# Revit family: Ytong stropní a střešní nosník
name_source: partatom
category: Konstrukční rámová konstrukce
units: mm (PartAtom-declared; Revit-internal decimal feet)

## family parameters
Materiál pro modelové chování = Jiné
Ořezat dutým tvarem při načtení = Ne
Sdílené = Ne
Tvar řezu = Není definováno
Vždy exportovat jako geometrii = Ne
Vždy vertikální = Ano
Založené na pracovní rovině = Ne
Zaokrouhlení délky rámové konstrukce = 0 mm
Zobrazit v půdorysech řeznou rovinu rodiny = Ano

## types (1)
- Ytong stropní a střešní nosník
    Autor = BIM Technology s.r.o.
    IfcExportAs = IfcBeam
    IfcExportType = JOIST
    Krátký popis = Stropní nosníky tvoří příhradová prostorová svařovaná výztuž zalitá do betonové patky obdélníkového průřezu s rozměry 120 × 40 mm.
    Materiál = beton
    Maximální délka nosníku = 8200 mm  [stored 26.9029 ft]
    Minimální délka nosníku = 1000 mm  [stored 3.28084 ft]
    Název tabulky = Ytong stropní a střešní nosník
    Odkaz na technický list = https://storefrontapi.commerce.xella.com
    Odkaz na web = https://www.xella.cz
    Popis = Stropní nosníky tvoří příhradová prostorová svařovaná výztuž zalitá do betonové patky obdélníkového průřezu s rozměry 120 × 40 mm.
    Požární odolnost = REI 120 DP1
    Skupina prvků = Skládaný strop
    Třída betonu = C 20/25
    URL = https://www.xella.cz
    Výrobce = Ytong
    Výška nosníku = 205 mm  [stored 0.672572 ft]
    Zobrazit ve výkazech = Ano
    Šířka nosníku = 120 mm  [stored 0.393701 ft]

note: [stored X ft] marks values corroborated as IEEE doubles in the binary element streams (Revit-internal decimal feet)
